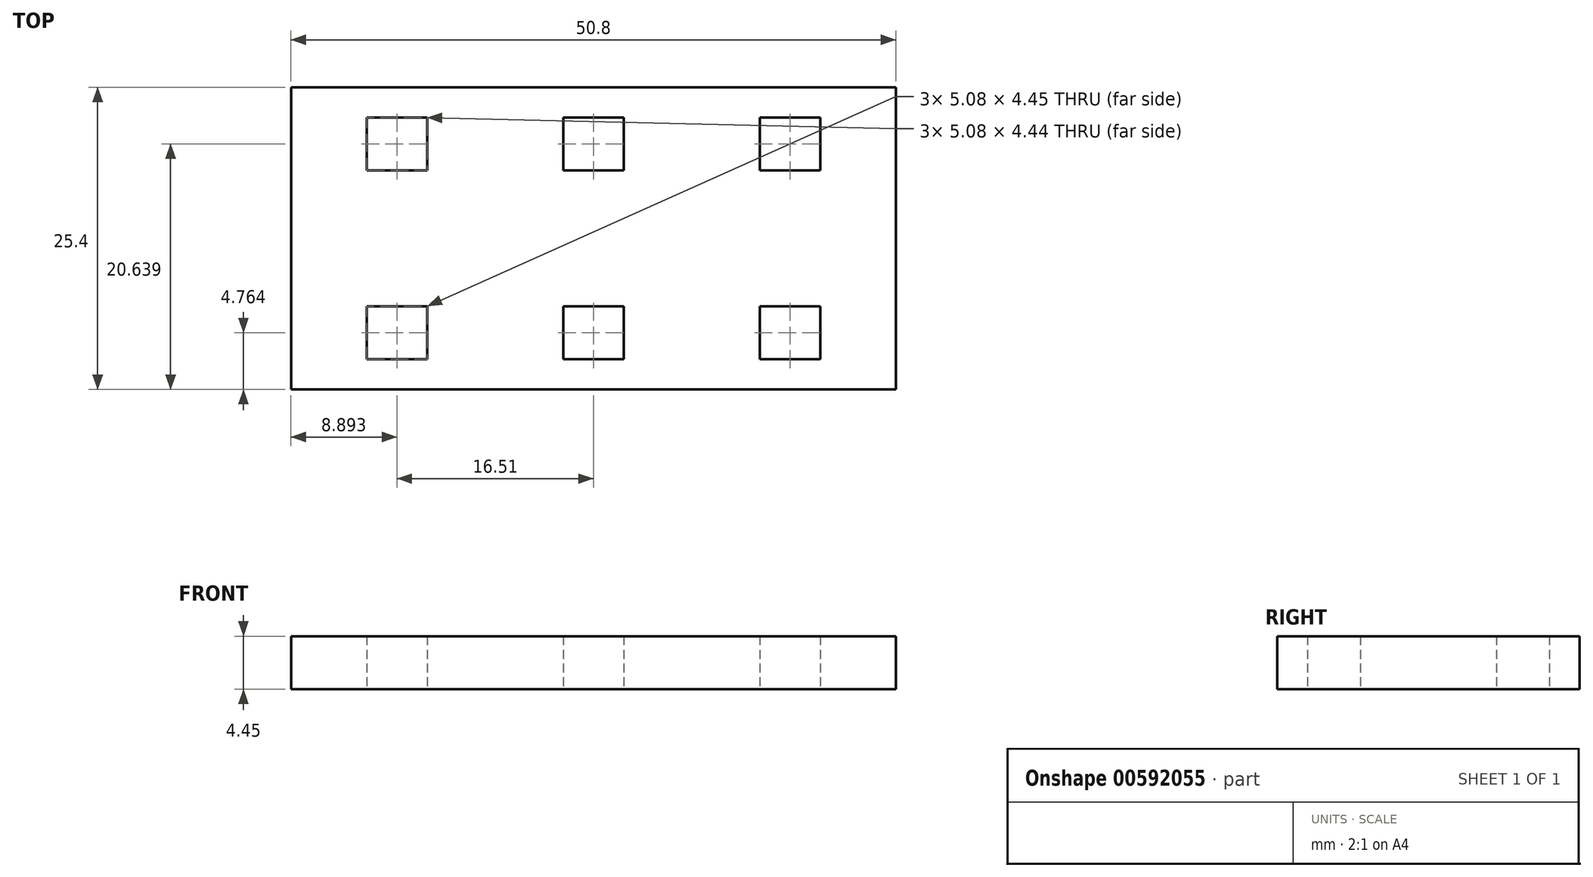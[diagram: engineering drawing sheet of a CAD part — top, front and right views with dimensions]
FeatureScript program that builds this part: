
annotation { "Feature Type Name" : "Feature", "Feature Type Description" : "" }
export const myFeature = defineFeature(function(context is Context, id is Id, definition is map)
    precondition{}
    {
        {
            var Q0;
            Q0=qCreatedBy(makeId("Top.planeOp"),FACE);
            var sketch = newSketch(context, id + "F0", { "sketchPlane" : qUnion([Q0])});
            skLineSegment(sketch, "E0.bottom", {"start": v(-20.77, 22.54) * mm, "end": v(30.03, 22.54) * mm});
            skLineSegment(sketch, "E0.top", {"start": v(-20.77, -2.86) * mm, "end": v(30.03, -2.86) * mm});
            skLineSegment(sketch, "E0.left", {"start": v(-20.77, 22.54) * mm, "end": v(-20.77, -2.86) * mm});
            skLineSegment(sketch, "E0.right", {"start": v(30.03, 22.54) * mm, "end": v(30.03, -2.86) * mm});
            skLineSegment(sketch, "E1.bottom", {"start": v(-14.42, 20) * mm, "end": v(-9.34, 20) * mm});
            skLineSegment(sketch, "E1.top", {"start": v(-14.42, 15.56) * mm, "end": v(-9.34, 15.56) * mm});
            skLineSegment(sketch, "E1.left", {"start": v(-14.42, 20) * mm, "end": v(-14.42, 15.56) * mm});
            skLineSegment(sketch, "E1.right", {"start": v(-9.34, 20) * mm, "end": v(-9.34, 15.56) * mm});
            skLineSegment(sketch, "E2.bottom", {"start": v(2.1, 20) * mm, "end": v(7.17, 20) * mm});
            skLineSegment(sketch, "E2.top", {"start": v(2.1, 15.56) * mm, "end": v(7.17, 15.56) * mm});
            skLineSegment(sketch, "E2.left", {"start": v(2.1, 20) * mm, "end": v(2.1, 15.56) * mm});
            skLineSegment(sketch, "E2.right", {"start": v(7.17, 20) * mm, "end": v(7.17, 15.56) * mm});
            skLineSegment(sketch, "E3.bottom", {"start": v(18.6, 20) * mm, "end": v(23.68, 20) * mm});
            skLineSegment(sketch, "E3.top", {"start": v(18.6, 15.56) * mm, "end": v(23.68, 15.56) * mm});
            skLineSegment(sketch, "E3.left", {"start": v(18.6, 20) * mm, "end": v(18.6, 15.56) * mm});
            skLineSegment(sketch, "E3.right", {"start": v(23.68, 20) * mm, "end": v(23.68, 15.56) * mm});
            skLineSegment(sketch, "E4", {"start": v(4.63, 20) * mm, "end": v(4.63, 15.56) * mm, "construction": true});
            skLineSegment(sketch, "E5", {"start": v(-20.77, 9.84) * mm, "end": v(30.03, 9.84) * mm, "construction": true});
            skLineSegment(sketch, "E6.MirrorCS", {"start": v(18.6, 4.13) * mm, "end": v(23.68, 4.13) * mm});
            skLineSegment(sketch, "E7.MirrorCS", {"start": v(18.6, -0.32) * mm, "end": v(18.6, 4.13) * mm});
            skLineSegment(sketch, "E8.MirrorCS", {"start": v(18.6, -0.32) * mm, "end": v(23.68, -0.32) * mm});
            skLineSegment(sketch, "E9.MirrorCS", {"start": v(23.68, -0.32) * mm, "end": v(23.68, 4.13) * mm});
            skLineSegment(sketch, "E10.MirrorCS", {"start": v(7.17, -0.32) * mm, "end": v(7.17, 4.13) * mm});
            skLineSegment(sketch, "E11.MirrorCS", {"start": v(2.1, -0.32) * mm, "end": v(7.17, -0.32) * mm});
            skLineSegment(sketch, "E12.MirrorCS", {"start": v(2.1, -0.32) * mm, "end": v(2.1, 4.13) * mm});
            skLineSegment(sketch, "E13.MirrorCS", {"start": v(2.1, 4.13) * mm, "end": v(7.17, 4.13) * mm});
            skLineSegment(sketch, "E14.MirrorCS", {"start": v(-9.34, -0.32) * mm, "end": v(-9.34, 4.13) * mm});
            skLineSegment(sketch, "E15.MirrorCS", {"start": v(-14.42, 4.13) * mm, "end": v(-9.34, 4.13) * mm});
            skLineSegment(sketch, "E16.MirrorCS", {"start": v(-14.42, -0.32) * mm, "end": v(-14.42, 4.13) * mm});
            skLineSegment(sketch, "E17.MirrorCS", {"start": v(-14.42, -0.32) * mm, "end": v(-9.34, -0.32) * mm});
            skSolve(sketch);
        }
        {
            var Q0;
            Q0=makeQuery(id+"F0.imprint","IMPRINT",FACE,{"disambiguationData":[TD([[makeQuery(id+"F0.imprint","IMPRINT",EDGE,{"derivedFrom":sQuery(id+"F0.wireOp",EDGE,"E0.bottom")}),-1.0]])]});
            extrude(context, id + "F1", {"entities" : qUnion([Q0]), "depth" : 4.44 * mm, "offsetDistance" : 25.4 * mm});
        }
    });
